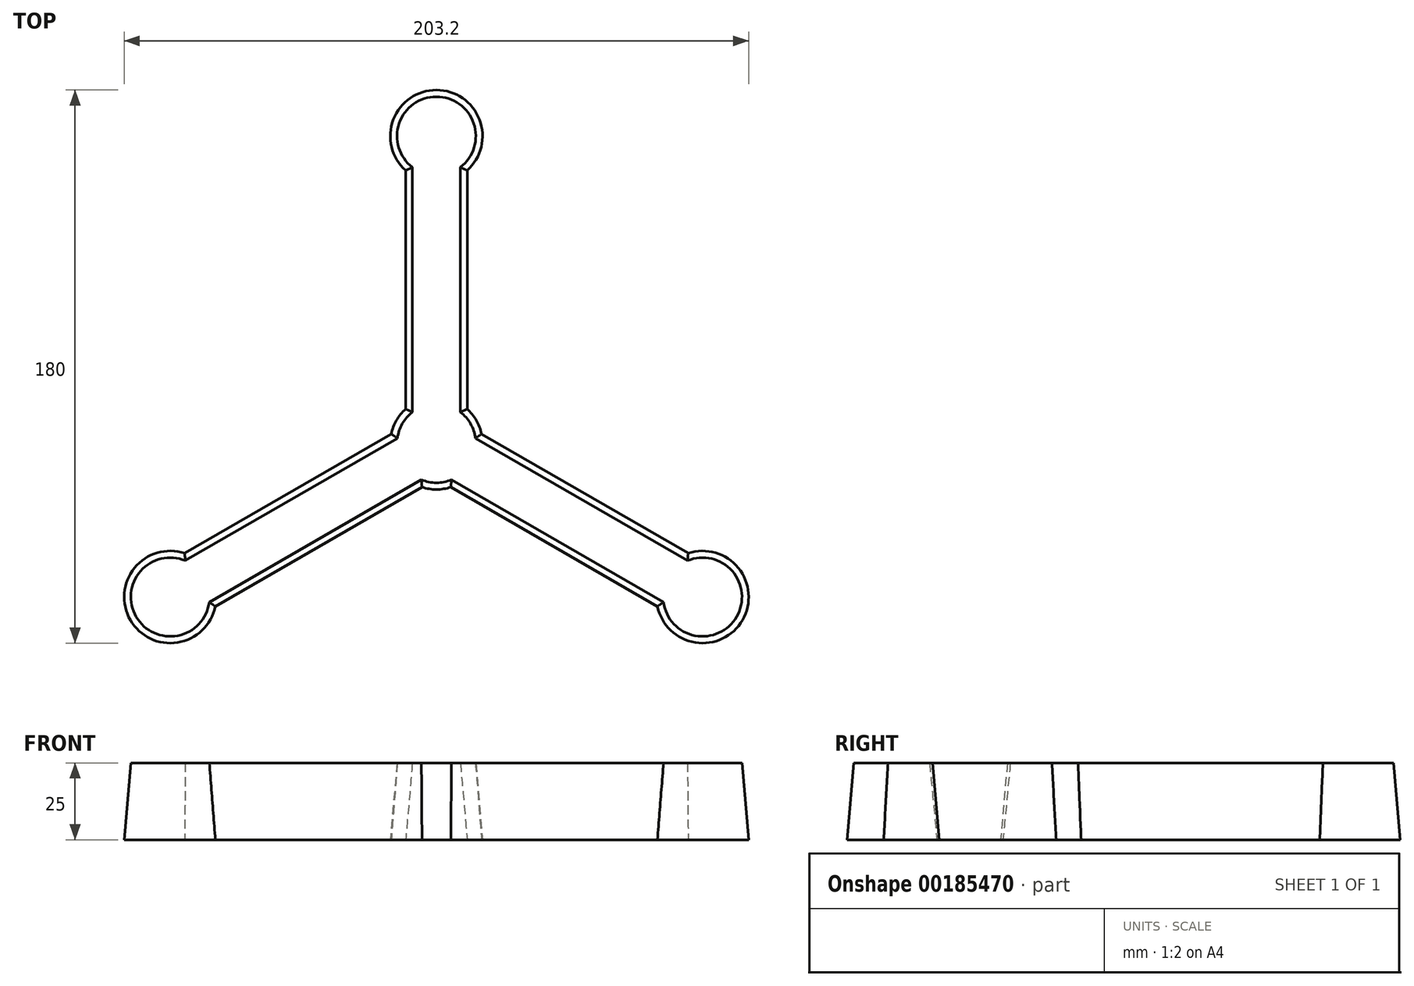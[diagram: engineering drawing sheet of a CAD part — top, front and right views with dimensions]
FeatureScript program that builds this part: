
annotation { "Feature Type Name" : "Feature", "Feature Type Description" : "" }
export const myFeature = defineFeature(function(context is Context, id is Id, definition is map)
    precondition{}
    {
        {
            var Q0;
            Q0=qCreatedBy(makeId("Top.planeOp"),FACE);
            var sketch = newSketch(context, id + "F0", { "sketchPlane" : qUnion([Q0])});
            skArc(sketch, "E0", {"start": v(-4.68, -14.25) * mm, "mid": v(0, -15) * mm, "end": v(4.68, -14.25) * mm});
            skArc(sketch, "E1", {"start": v(10, 88.82) * mm, "mid": v(0, 115) * mm, "end": v(-10, 88.82) * mm});
            skLineSegment(sketch, "E2", {"start": v(0, 100) * mm, "end": v(0, 0) * mm, "construction": true});
            skLineSegment(sketch, "E3.0", {"start": v(-10, 88.82) * mm, "end": v(-10, 11.18) * mm});
            skLineSegment(sketch, "E4.0", {"start": v(10, 88.82) * mm, "end": v(10, 11.18) * mm});
            skArc(sketch, "E5.1.0", {"start": v(-81.92, -35.75) * mm, "mid": v(-99.6, -57.5) * mm, "end": v(-71.92, -53.07) * mm});
            skLineSegment(sketch, "E5.1.1", {"start": v(-71.92, -53.07) * mm, "end": v(-4.68, -14.25) * mm});
            skLineSegment(sketch, "E5.1.2", {"start": v(-81.92, -35.75) * mm, "end": v(-14.68, 3.07) * mm});
            skArc(sketch, "E5.2.0", {"start": v(71.92, -53.07) * mm, "mid": v(99.6, -57.5) * mm, "end": v(81.92, -35.75) * mm});
            skLineSegment(sketch, "E5.2.1", {"start": v(81.92, -35.75) * mm, "end": v(14.68, 3.07) * mm});
            skLineSegment(sketch, "E5.2.2", {"start": v(71.92, -53.07) * mm, "end": v(4.68, -14.25) * mm});
            skArc(sketch, "E6.trimOffspring", {"start": v(14.68, 3.07) * mm, "mid": v(13, 7.5) * mm, "end": v(10, 11.18) * mm});
            skArc(sketch, "E7.trimOffspring", {"start": v(-10, 11.18) * mm, "mid": v(-13, 7.5) * mm, "end": v(-14.68, 3.07) * mm});
            skSolve(sketch);
        }
        {
            var Q0;
            Q0 = qSketchRegion(id + "F0", true);
            extrude(context, id + "F1", {"entities" : qUnion([Q0]), "depth" : 25 * mm, "hasDraft" : true, "draftAngle" : 5 * degree, "draftPullDirection" : true});
        }
    });
